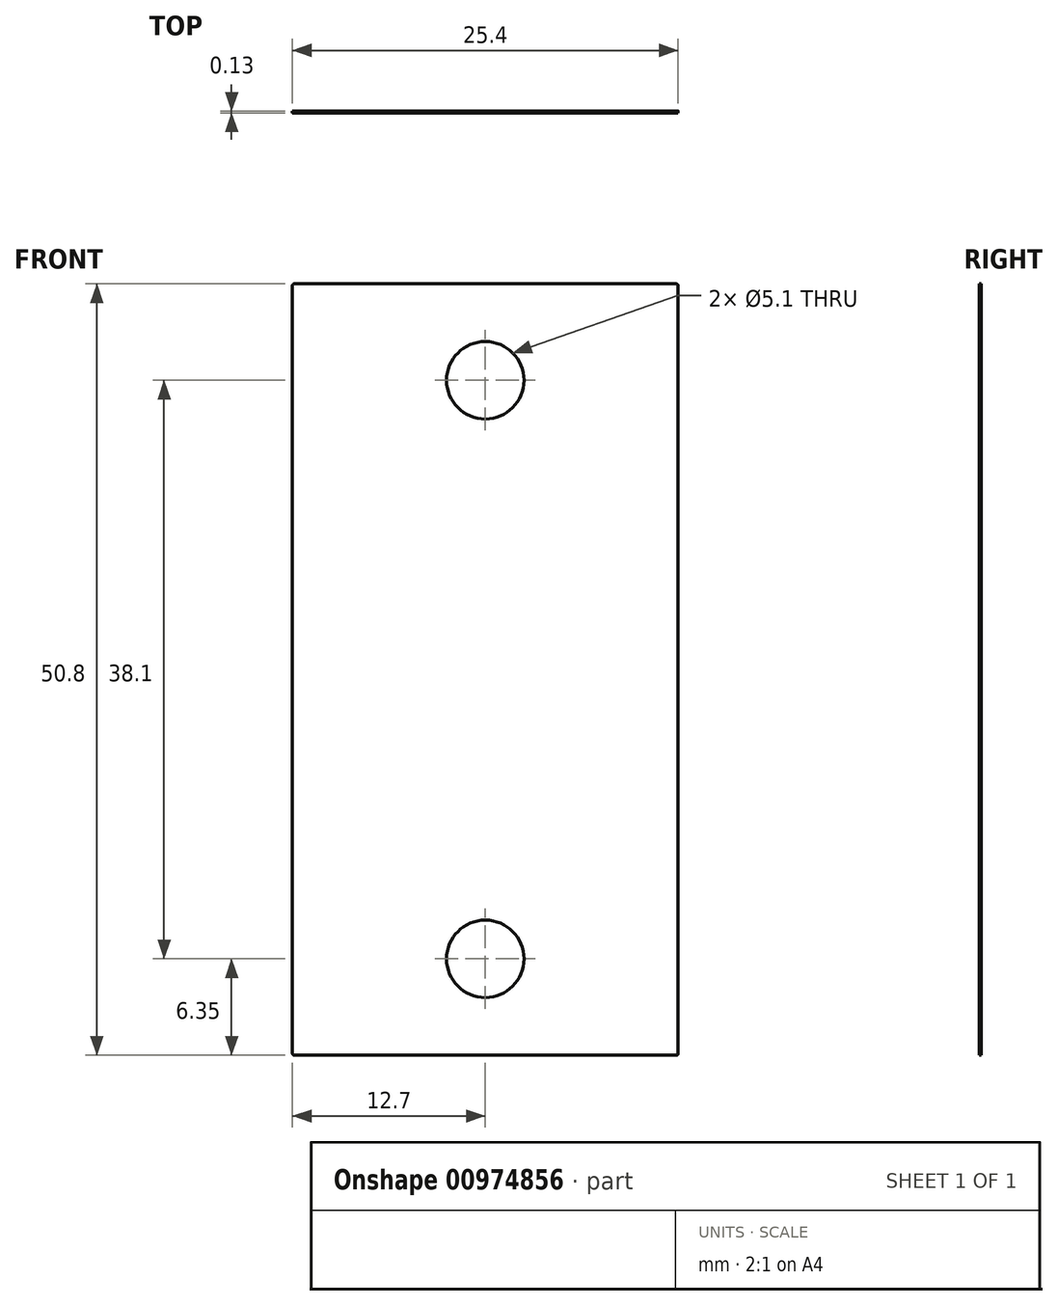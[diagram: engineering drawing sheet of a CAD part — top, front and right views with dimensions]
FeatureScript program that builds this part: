
annotation { "Feature Type Name" : "Feature", "Feature Type Description" : "" }
export const myFeature = defineFeature(function(context is Context, id is Id, definition is map)
    precondition{}
    {
        {
            assignVariable(context, id + "F0", {"name" : "thin_mdf_thickness", "anyValue" : 1 / 8});
        }
        {
            var Q0;
            Q0=qCreatedBy(makeId("Front.planeOp"),FACE);
            var sketch = newSketch(context, id + "F1", { "sketchPlane" : qUnion([Q0])});
            skLineSegment(sketch, "E0.bottom", {"start": v(12.7, 25.4) * mm, "end": v(-12.7, 25.4) * mm});
            skLineSegment(sketch, "E0.top", {"start": v(12.7, -25.4) * mm, "end": v(-12.7, -25.4) * mm});
            skLineSegment(sketch, "E0.left", {"start": v(12.7, 25.4) * mm, "end": v(12.7, -25.4) * mm});
            skLineSegment(sketch, "E0.right", {"start": v(-12.7, 25.4) * mm, "end": v(-12.7, -25.4) * mm});
            skPoint(sketch, "E0.middle", {"position": v(0, 0) * mm});
            skLineSegment(sketch, "E1", {"start": v(0, -25.4) * mm, "end": v(0, 25.4) * mm, "construction": true});
            skLineSegment(sketch, "E2", {"start": v(0, -25.4) * mm, "end": v(0, -12.7) * mm, "construction": true});
            skLineSegment(sketch, "E3", {"start": v(0, -12.7) * mm, "end": v(0, 12.7) * mm, "construction": true});
            skLineSegment(sketch, "E4", {"start": v(0, 12.7) * mm, "end": v(0, 25.4) * mm, "construction": true});
            skCircle(sketch, "E5", {"center": v(0, 19.05) * mm, "radius": 2.55 * mm});
            skCircle(sketch, "E6", {"center": v(0, -19.05) * mm, "radius": 2.55 * mm});
            skSolve(sketch);
        }
        {
            var Q0;
            Q0=makeQuery(id+"F1.imprint","IMPRINT",FACE,{"disambiguationData":[TD([[makeQuery(id+"F1.imprint","IMPRINT",EDGE,{"derivedFrom":sQuery(id+"F1.wireOp",EDGE,"E0.bottom")}),1.0]])]});
            extrude(context, id + "F2", {"entities" : qUnion([Q0]), "depth" : (getVariable(context, 'thin_mdf_thickness')) * mm, "offsetDistance" : 25.4 * mm});
        }
        {
            var Q0;
            Q0=makeQuery(id+"F2.opExtrude","SWEPT_EDGE",EDGE,{"disambiguationData":[OSD([sQuery(id+"F1.wireOp",EDGE,"E0.bottom"),sQuery(id+"F1.wireOp",EDGE,"E0.right")])]});
            var Q1;
            Q1=makeQuery(id+"F2.opExtrude","SWEPT_EDGE",EDGE,{"disambiguationData":[OSD([sQuery(id+"F1.wireOp",EDGE,"E0.bottom"),sQuery(id+"F1.wireOp",EDGE,"E0.left")])]});
            var Q2;
            Q2=makeQuery(id+"F2.opExtrude","SWEPT_EDGE",EDGE,{"disambiguationData":[OSD([sQuery(id+"F1.wireOp",EDGE,"E0.top"),sQuery(id+"F1.wireOp",EDGE,"E0.left")])]});
            var Q3;
            Q3=makeQuery(id+"F2.opExtrude","SWEPT_EDGE",EDGE,{"disambiguationData":[OSD([sQuery(id+"F1.wireOp",EDGE,"E0.top"),sQuery(id+"F1.wireOp",EDGE,"E0.right")])]});
            fillet(context, id + "F3", {"entities" : qUnion([Q0, Q1, Q2, Q3]), "radius" : (getVariable(context, 'thin_mdf_thickness')) * mm, "tangentPropagation" : true, "allowEdgeOverflow" : false});
        }
    });
